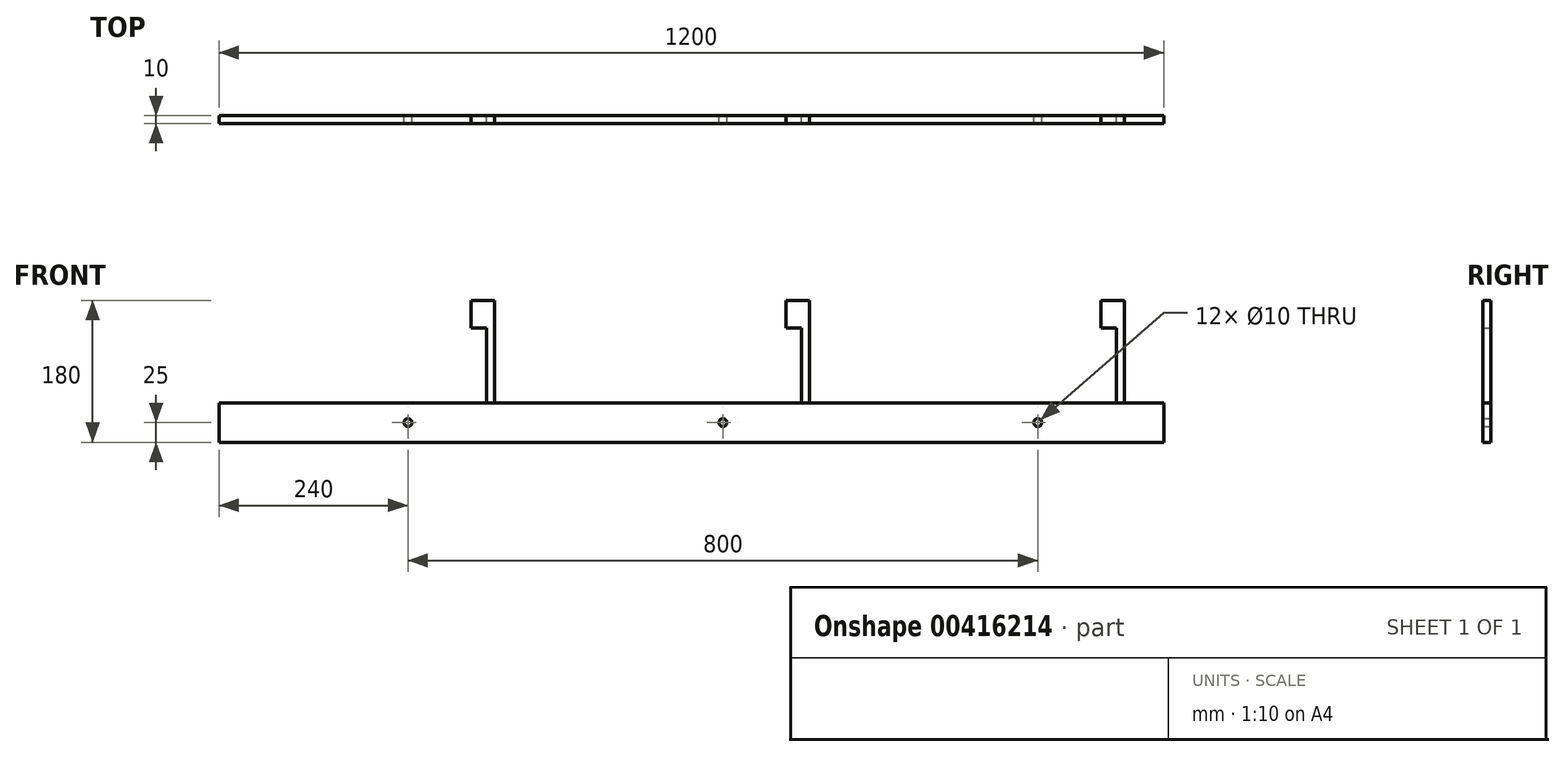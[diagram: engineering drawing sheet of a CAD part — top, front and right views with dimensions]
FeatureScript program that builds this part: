
annotation { "Feature Type Name" : "Feature", "Feature Type Description" : "" }
export const myFeature = defineFeature(function(context is Context, id is Id, definition is map)
    precondition{}
    {
        {
            var Q0;
            Q0=qCreatedBy(makeId("Front.planeOp"),FACE);
            var sketch = newSketch(context, id + "F0", { "sketchPlane" : qUnion([Q0])});
            skLineSegment(sketch, "E0", {"start": v(-600, 0) * mm, "end": v(600, 0) * mm});
            skLineSegment(sketch, "E1", {"start": v(600, 0) * mm, "end": v(600, 50) * mm});
            skLineSegment(sketch, "E2", {"start": v(600, 50) * mm, "end": v(-600, 50) * mm});
            skLineSegment(sketch, "E3", {"start": v(-600, 0) * mm, "end": v(-600, 50) * mm});
            skSolve(sketch);
        }
        {
            var Q0;
            Q0=qCreatedBy(makeId("Front.planeOp"),FACE);
            var sketch = newSketch(context, id + "F1", { "sketchPlane" : qUnion([Q0])});
            skLineSegment(sketch, "E4", {"start": v(550, 50) * mm, "end": v(550, 180) * mm});
            skLineSegment(sketch, "E5", {"start": v(550, 180) * mm, "end": v(520, 180) * mm});
            skLineSegment(sketch, "E6", {"start": v(520, 180) * mm, "end": v(520, 145) * mm});
            skLineSegment(sketch, "E7", {"start": v(520, 145) * mm, "end": v(540, 145) * mm});
            skLineSegment(sketch, "E8", {"start": v(540, 145) * mm, "end": v(540, 50) * mm});
            skLineSegment(sketch, "E9", {"start": v(540, 50) * mm, "end": v(550, 50) * mm});
            skLineSegment(sketch, "E10.1.0.0", {"start": v(150, 180) * mm, "end": v(120, 180) * mm});
            skLineSegment(sketch, "E10.1.0.1", {"start": v(140, 145) * mm, "end": v(140, 50) * mm});
            skLineSegment(sketch, "E10.1.0.2", {"start": v(120, 180) * mm, "end": v(120, 145) * mm});
            skLineSegment(sketch, "E10.1.0.3", {"start": v(150, 50) * mm, "end": v(150, 180) * mm});
            skLineSegment(sketch, "E10.1.0.4", {"start": v(120, 145) * mm, "end": v(140, 145) * mm});
            skLineSegment(sketch, "E10.1.0.5", {"start": v(140, 50) * mm, "end": v(150, 50) * mm});
            skLineSegment(sketch, "E10.2.0.0", {"start": v(-250, 180) * mm, "end": v(-280, 180) * mm});
            skLineSegment(sketch, "E10.2.0.1", {"start": v(-260, 145) * mm, "end": v(-260, 50) * mm});
            skLineSegment(sketch, "E10.2.0.2", {"start": v(-280, 180) * mm, "end": v(-280, 145) * mm});
            skLineSegment(sketch, "E10.2.0.3", {"start": v(-250, 50) * mm, "end": v(-250, 180) * mm});
            skLineSegment(sketch, "E10.2.0.4", {"start": v(-280, 145) * mm, "end": v(-260, 145) * mm});
            skLineSegment(sketch, "E10.2.0.5", {"start": v(-260, 50) * mm, "end": v(-250, 50) * mm});
            skLineSegment(sketch, "E10.direction1", {"start": v(240, 50) * mm, "end": v(-160, 50) * mm, "construction": true});
            skSolve(sketch);
        }
        {
            var Q0;
            Q0 = qSketchRegion(id + "F0", true);
            var Q1;
            Q1 = qSketchRegion(id + "F1", true);
            extrude(context, id + "F2", {"entities" : qUnion([Q0, Q1]), "depth" : 10 * mm});
        }
        {
            var Q0;
            Q0=qCreatedBy(makeId("Front.planeOp"),FACE);
            var sketch = newSketch(context, id + "F3", { "sketchPlane" : qUnion([Q0])});
            skCircle(sketch, "E11", {"center": v(440, 25) * mm, "radius": 5 * mm});
            skCircle(sketch, "E12.1.0.0", {"center": v(40, 25) * mm, "radius": 5 * mm});
            skCircle(sketch, "E12.2.0.0", {"center": v(-360, 25) * mm, "radius": 5 * mm});
            skLineSegment(sketch, "E12.direction1", {"start": v(440, 25) * mm, "end": v(40, 25) * mm, "construction": true});
            skSolve(sketch);
        }
        {
            var Q0;
            Q0 = qSketchRegion(id + "F3", true);
            var Q1;
            Q1=makeQuery(id+"F2.opExtrude","CAP_FACE",FACE,{"disambiguationData":[OSD([sQuery(id+"F0.wireOp",EDGE,"E0"),sQuery(id+"F0.wireOp",EDGE,"E1"),sQuery(id+"F0.wireOp",EDGE,"E2"),sQuery(id+"F0.wireOp",EDGE,"E3")])],"isStart":false});
            extrude(context, id + "F4", {"entities" : qUnion([Q0]), "operationType" : NewBodyOperationType.REMOVE, "endBound" : BoundingType.UP_TO_SURFACE, "endBoundEntityFace" : qUnion([Q1]), "depth" : 25 * mm});
        }
    });
